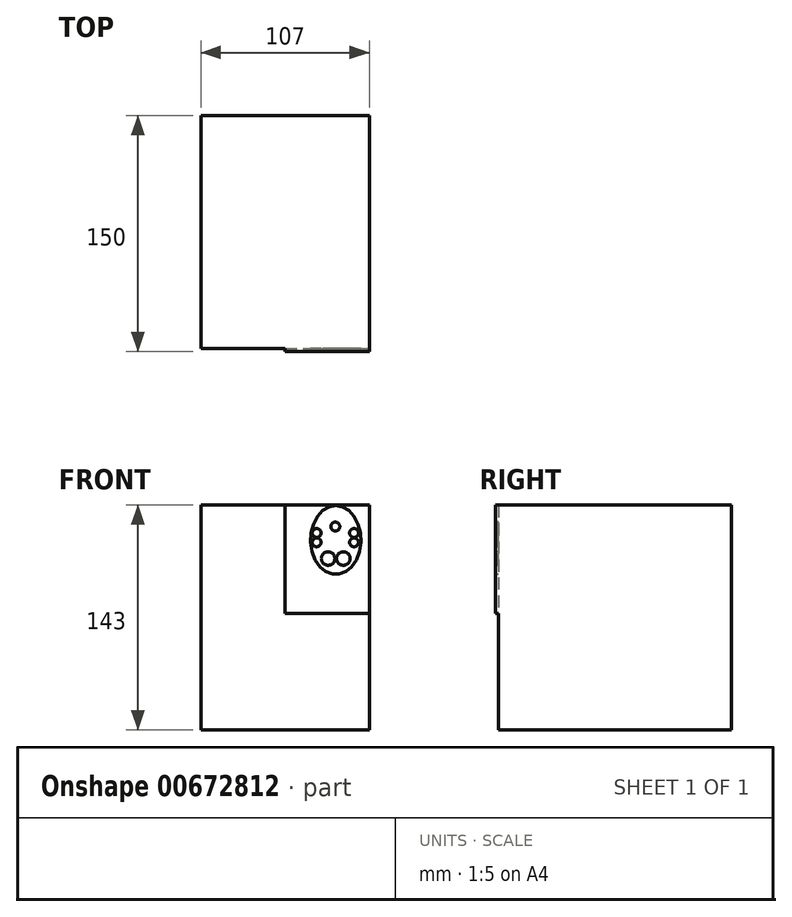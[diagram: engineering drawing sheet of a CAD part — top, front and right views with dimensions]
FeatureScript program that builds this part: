
annotation { "Feature Type Name" : "Feature", "Feature Type Description" : "" }
export const myFeature = defineFeature(function(context is Context, id is Id, definition is map)
    precondition{}
    {
        {
            var Q0;
            Q0=qCreatedBy(makeId("Front.planeOp"),FACE);
            var sketch = newSketch(context, id + "F0", { "sketchPlane" : qUnion([Q0])});
            skLineSegment(sketch, "E0.bottom", {"start": v(53.5, 71.5) * mm, "end": v(-53.5, 71.5) * mm});
            skLineSegment(sketch, "E0.top", {"start": v(53.5, -71.5) * mm, "end": v(-53.5, -71.5) * mm});
            skLineSegment(sketch, "E0.left", {"start": v(53.5, 71.5) * mm, "end": v(53.5, -71.5) * mm});
            skLineSegment(sketch, "E0.right", {"start": v(-53.5, 71.5) * mm, "end": v(-53.5, -71.5) * mm});
            skPoint(sketch, "E0.middle", {"position": v(0, 0) * mm});
            skSolve(sketch);
        }
        {
            var Q0;
            Q0=makeQuery(id+"F0.imprint","IMPRINT",FACE,{"disambiguationData":[TD([[makeQuery(id+"F0.imprint","IMPRINT",EDGE,{"derivedFrom":sQuery(id+"F0.wireOp",EDGE,"E0.bottom")}),1.0]])]});
            extrude(context, id + "F1", {"entities" : qUnion([Q0]), "depth" : 150 * mm, "offsetDistance" : 25 * mm});
        }
        {
            var Q0;
            Q0=makeQuery(id+"F1.opExtrude","CAP_FACE",FACE,{"disambiguationData":[OSD([sQuery(id+"F0.wireOp",EDGE,"E0.bottom"),sQuery(id+"F0.wireOp",EDGE,"E0.top"),sQuery(id+"F0.wireOp",EDGE,"E0.left"),sQuery(id+"F0.wireOp",EDGE,"E0.right")])],"isStart":false});
            var sketch = newSketch(context, id + "F2", { "sketchPlane" : qUnion([Q0])});
            skEllipse(sketch, "E1", {"center": v(32.16, 49.25) * mm, "majorRadius": 21.83 * mm, "minorRadius": 16.04 * mm, "majorAxis": v(0, 1)});
            skEllipse(sketch, "E2", {"center": v(31.88, 54.9) * mm, "majorRadius": 29.93 * mm, "minorRadius": 19.27 * mm, "majorAxis": v(0, 1)});
            skCircle(sketch, "E3", {"center": v(27.27, 37.51) * mm, "radius": 4.32 * mm});
            skCircle(sketch, "E4.MirrorC", {"center": v(37.04, 37.51) * mm, "radius": 4.32 * mm});
            skCircle(sketch, "E5", {"center": v(20.03, 47.78) * mm, "radius": 2.8 * mm});
            skCircle(sketch, "E6.MirrorC", {"center": v(20.03, 53.77) * mm, "radius": 2.8 * mm});
            skCircle(sketch, "E7.MirrorC", {"center": v(43.73, 47.78) * mm, "radius": 2.8 * mm});
            skCircle(sketch, "E8.MirrorC", {"center": v(43.73, 53.77) * mm, "radius": 2.8 * mm});
            skCircle(sketch, "E9", {"center": v(31.88, 57.8) * mm, "radius": 2.85 * mm});
            skLineSegment(sketch, "E10.bottom", {"start": v(0, 71.5) * mm, "end": v(65.4, 71.5) * mm});
            skLineSegment(sketch, "E10.top", {"start": v(0, 2.74) * mm, "end": v(65.4, 2.74) * mm});
            skLineSegment(sketch, "E10.left", {"start": v(0, 71.5) * mm, "end": v(0, 2.74) * mm});
            skLineSegment(sketch, "E10.right", {"start": v(65.4, 71.5) * mm, "end": v(65.4, 2.74) * mm});
            skSolve(sketch);
        }
        {
            var Q0;
            Q0=makeQuery(id+"F2.imprint","IMPRINT",FACE,{"disambiguationData":[TD([[makeQuery(id+"F2.imprint","IMPRINT",EDGE,{"derivedFrom":makeQuery(id+"F1.opExtrude","CAP_EDGE",EDGE,{"disambiguationData":[OSD([sQuery(id+"F0.wireOp",EDGE,"E0.top")])],"isStart":false})}),-1.0]])]});
            var Q1;
            Q1=makeQuery(id+"F2.imprint","IMPRINT",FACE,{"disambiguationData":[TD([[makeQuery(id+"F2.imprint","IMPRINT",EDGE,{"derivedFrom":sQuery(id+"F2.wireOp",EDGE,"E1")}),1.0]])]});
            extrude(context, id + "F3", {"entities" : qUnion([Q0, Q1]), "operationType" : NewBodyOperationType.REMOVE, "oppositeDirection" : true, "depth" : 2 * mm, "offsetDistance" : 25 * mm});
        }
    });
